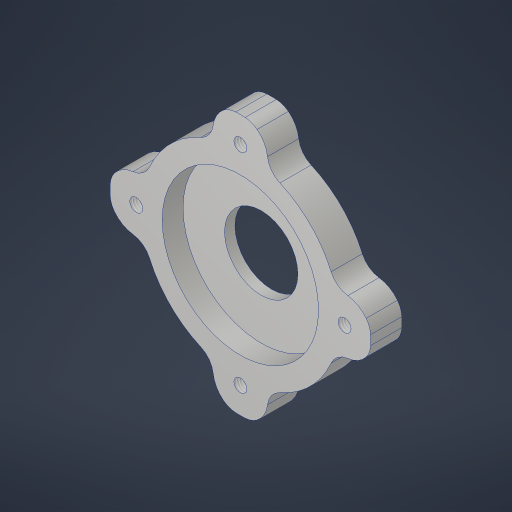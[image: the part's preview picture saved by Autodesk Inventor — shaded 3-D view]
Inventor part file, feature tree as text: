
AUTODESK INVENTOR PART (.ipt)
format: ipt  version: 2023.4 (Build 274418000, 418)  size: 278,528 bytes
history: native  units: in
note: dims shown in document units (in); Inventor stores cm internally (conversion verified against a paired STEP export)
features: extrude x3, sketch x2, hole x1, mirror x1, fillet x1, projected_geometry x1
ambient origin geometry x8: Origin, YZ Plane, XZ Plane, XY Plane, X Axis, Y Axis, Z Axis, Center Point
bodies: Solid1 (feature_tree)
feature tree (9):
  sketch  "Sketch1"  dims[d0=1.875in d1=0.625in]
  extrude  "Extrusion1"  Depth=0.625in
  extrude  "Extrusion2"  Depth=0.375in TaperAngle=0.0deg
  hole  "Hole1"  [1 undecoded]
  extrude  "Extrusion3"  Depth=0.25in TaperAngle=0.0deg
  mirror  "Mirror1"
  fillet  "Fillet1"  Radius=0.25in
  sketch  "Sketch2"  dims[d2=2.5in d3=0.375in d4=0.0in d5=0.88in d6=0.25in d7=0.0in d8=0.156in d9=0.38in d10=0.385in d11=0.25in d12=0.5635in d13=1.0in d14=0.8108in d15=0.25in d16=0.25in d17=0.25in d18=0.25in d19=0.25in d20=45.0deg d21=0.25in d22=45.0deg d23=0.25in d24=0.0in d25=0.25in d26=0.25in d27=0.25in]
  projected_geometry  "Project Cut Edges1"
note: 1 required parameter value undecoded (feature->parameter linkage not recoverable at this tier; creation-order binding heuristic only, values carry confidence <= 0.55)
